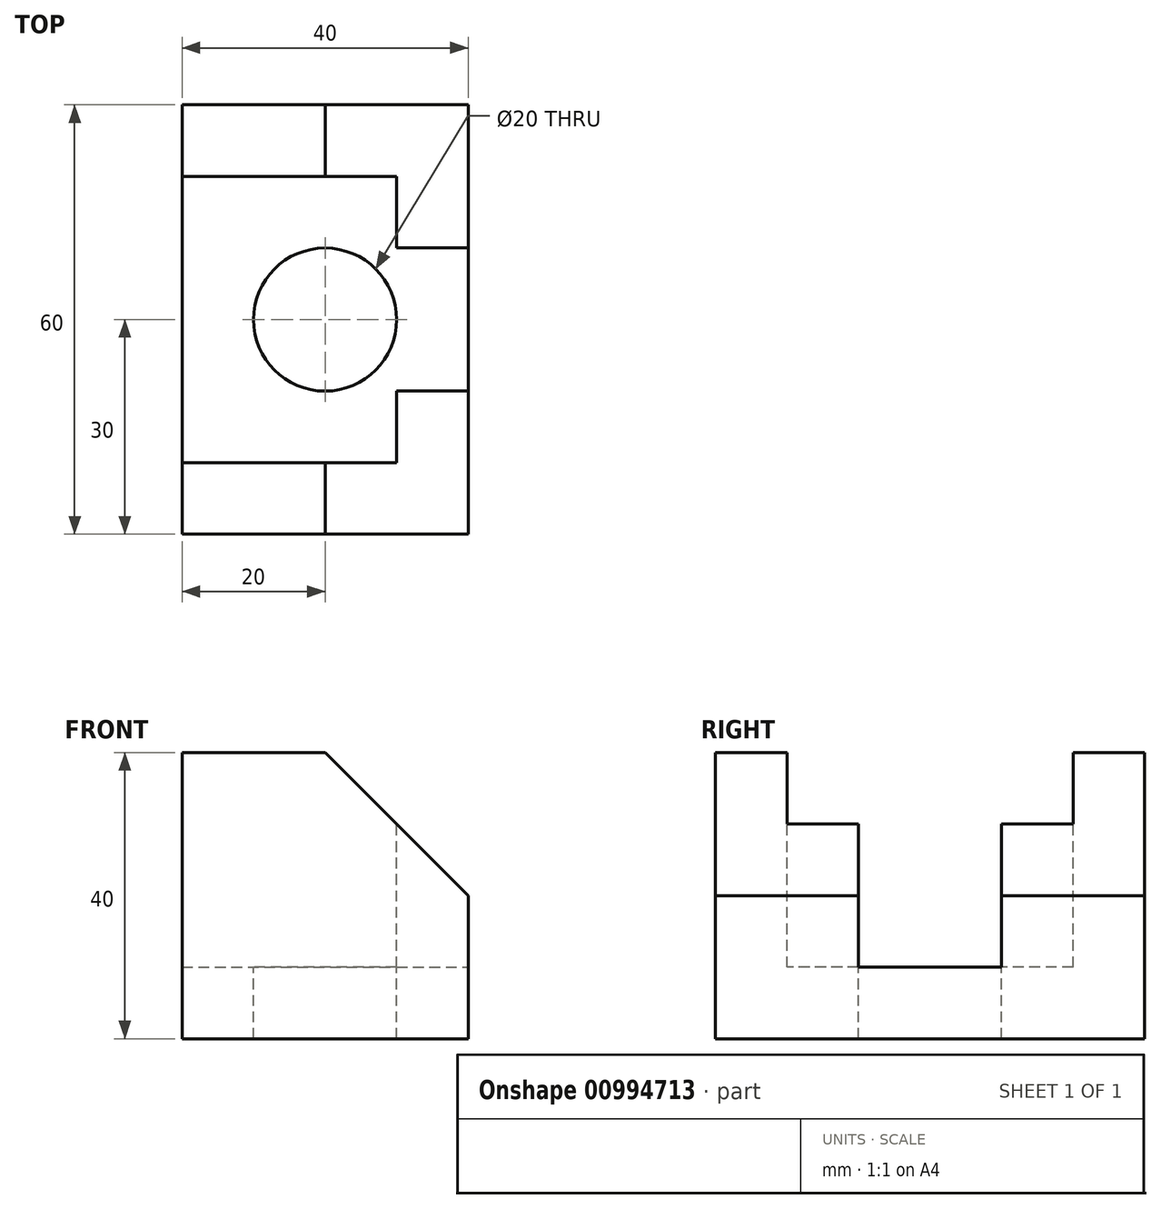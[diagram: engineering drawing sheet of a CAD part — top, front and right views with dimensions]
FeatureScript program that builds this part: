
annotation { "Feature Type Name" : "Feature", "Feature Type Description" : "" }
export const myFeature = defineFeature(function(context is Context, id is Id, definition is map)
    precondition{}
    {
        {
            var Q0;
            Q0=qCreatedBy(makeId("Front.planeOp"),FACE);
            var sketch = newSketch(context, id + "F0", { "sketchPlane" : qUnion([Q0])});
            skLineSegment(sketch, "E0", {"start": v(-20, 0) * mm, "end": v(-20, 40) * mm});
            skLineSegment(sketch, "E1", {"start": v(-20, 40) * mm, "end": v(0, 40) * mm});
            skLineSegment(sketch, "E2", {"start": v(0, 40) * mm, "end": v(20, 20) * mm});
            skLineSegment(sketch, "E3", {"start": v(20, 20) * mm, "end": v(20, 0) * mm});
            skLineSegment(sketch, "E4", {"start": v(20, 0) * mm, "end": v(-20, 0) * mm});
            skSolve(sketch);
        }
        {
            var Q0;
            Q0=makeQuery(id+"F0.imprint","IMPRINT",FACE,{"disambiguationData":[TD([[makeQuery(id+"F0.imprint","IMPRINT",EDGE,{"derivedFrom":sQuery(id+"F0.wireOp",EDGE,"E0")}),-1.0]])]});
            extrude(context, id + "F1", {"entities" : qUnion([Q0]), "endBound" : BoundingType.SYMMETRIC, "oppositeDirection" : true, "depth" : 60 * mm, "offsetDistance" : 25 * mm});
        }
        {
            var Q0;
            Q0=makeQuery(id+"F1.opExtrude","SWEPT_FACE",FACE,{"disambiguationData":[OSD([sQuery(id+"F0.wireOp",EDGE,"E1")])]});
            var sketch = newSketch(context, id + "F2", { "sketchPlane" : qUnion([Q0])});
            skLineSegment(sketch, "E5.bottom", {"start": v(-20, 20) * mm, "end": v(10, 20) * mm});
            skLineSegment(sketch, "E5.top", {"start": v(-20, -20) * mm, "end": v(10, -20) * mm});
            skLineSegment(sketch, "E5.left", {"start": v(-20, 20) * mm, "end": v(-20, -20) * mm});
            skLineSegment(sketch, "E5.right", {"start": v(10, 20) * mm, "end": v(10, 10) * mm});
            skLineSegment(sketch, "E6", {"start": v(10, -10) * mm, "end": v(20, -10) * mm});
            skLineSegment(sketch, "E7", {"start": v(20, -10) * mm, "end": v(20, 10) * mm});
            skLineSegment(sketch, "E8", {"start": v(20, 10) * mm, "end": v(10, 10) * mm});
            skLineSegment(sketch, "E9.trimOffspring", {"start": v(10, -10) * mm, "end": v(10, -20) * mm});
            skSolve(sketch);
        }
        {
            var Q0;
            Q0 = qSketchRegion(id + "F2", true);
            extrude(context, id + "F3", {"entities" : qUnion([Q0]), "operationType" : NewBodyOperationType.REMOVE, "oppositeDirection" : true, "depth" : 30 * mm, "offsetDistance" : 25 * mm});
        }
        {
            var Q0;
            Q0=makeQuery(id+"F3.boolean.opBoolean","COPY",FACE,{"derivedFrom":makeQuery(id+"F3.opExtrude","CAP_FACE",FACE,{"disambiguationData":[OSD([sQuery(id+"F2.wireOp",EDGE,"E5.bottom"),sQuery(id+"F2.wireOp",EDGE,"E5.top"),sQuery(id+"F2.wireOp",EDGE,"E5.left"),sQuery(id+"F2.wireOp",EDGE,"E5.right"),sQuery(id+"F2.wireOp",EDGE,"E6"),sQuery(id+"F2.wireOp",EDGE,"E7"),sQuery(id+"F2.wireOp",EDGE,"E8"),sQuery(id+"F2.wireOp",EDGE,"E9.trimOffspring")])],"isStart":false})});
            var sketch = newSketch(context, id + "F4", { "sketchPlane" : qUnion([Q0])});
            skCircle(sketch, "E10", {"center": v(0, 0) * mm, "radius": 10 * mm});
            skSolve(sketch);
        }
        {
            var Q0;
            Q0=makeQuery(id+"F4.imprint","IMPRINT",FACE,{"disambiguationData":[TD([[makeQuery(id+"F4.imprint","IMPRINT",EDGE,{"derivedFrom":sQuery(id+"F4.wireOp",EDGE,"E10")}),1.0]])]});
            extrude(context, id + "F5", {"entities" : qUnion([Q0]), "operationType" : NewBodyOperationType.REMOVE, "oppositeDirection" : true, "depth" : 10 * mm, "offsetDistance" : 25 * mm});
        }
    });
